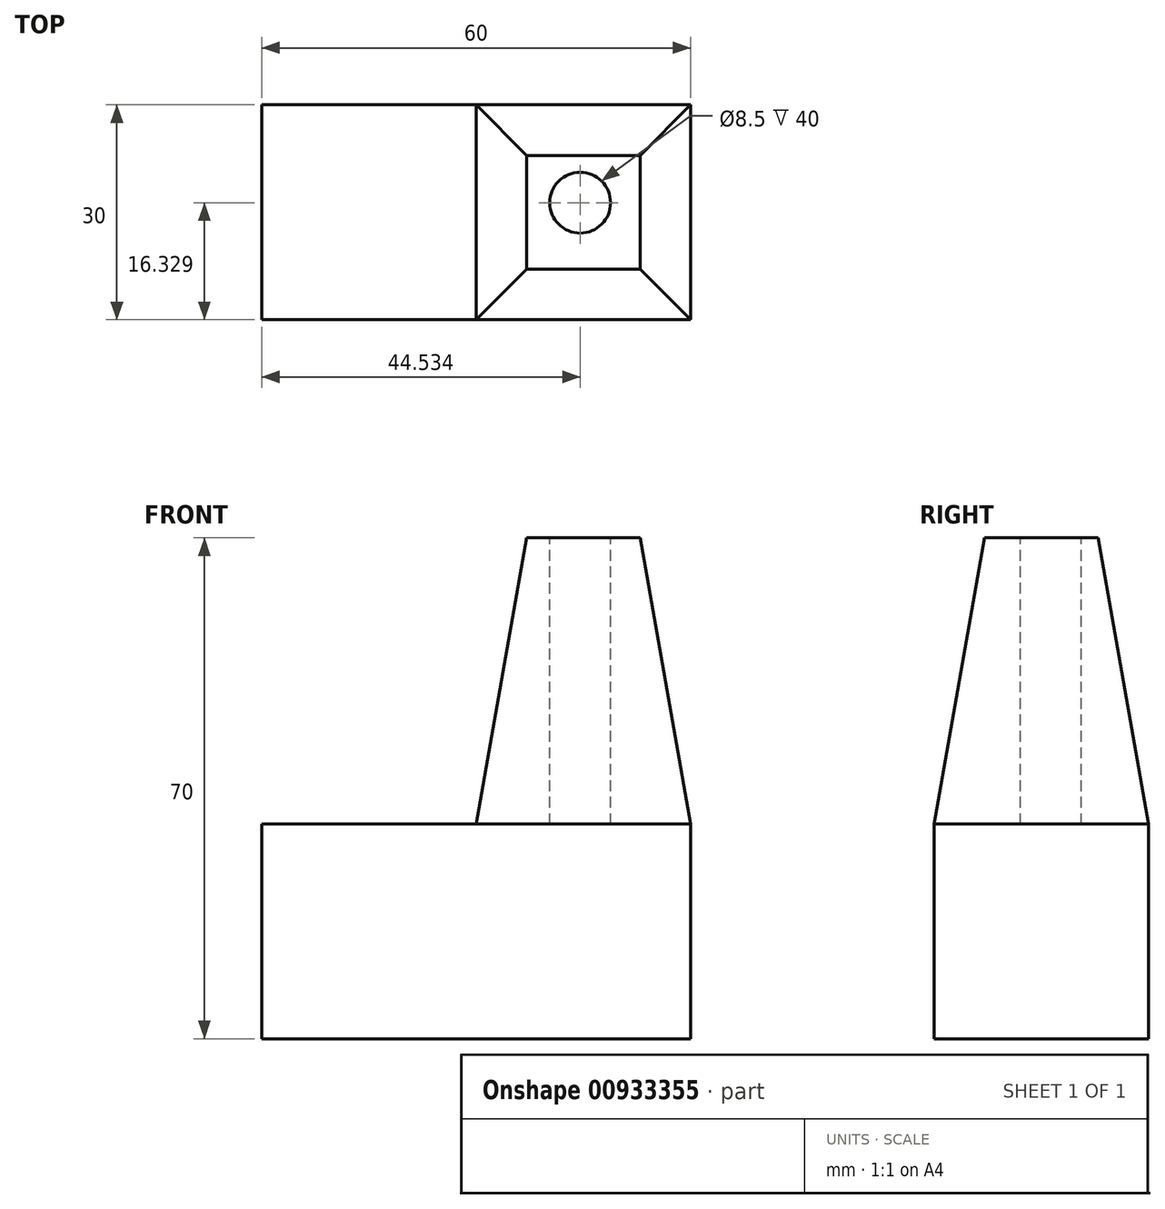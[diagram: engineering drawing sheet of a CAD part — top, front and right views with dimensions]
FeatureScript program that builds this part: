
annotation { "Feature Type Name" : "Feature", "Feature Type Description" : "" }
export const myFeature = defineFeature(function(context is Context, id is Id, definition is map)
    precondition{}
    {
        {
            var Q0;
            Q0=qCreatedBy(makeId("Front.planeOp"),FACE);
            var sketch = newSketch(context, id + "F0", { "sketchPlane" : qUnion([Q0])});
            skLineSegment(sketch, "E0.bottom", {"start": v(30, -15) * mm, "end": v(-30, -15) * mm});
            skLineSegment(sketch, "E0.top", {"start": v(30, 15) * mm, "end": v(-30, 15) * mm});
            skLineSegment(sketch, "E0.left", {"start": v(30, -15) * mm, "end": v(30, 15) * mm});
            skLineSegment(sketch, "E0.right", {"start": v(-30, -15) * mm, "end": v(-30, 15) * mm});
            skPoint(sketch, "E0.middle", {"position": v(0, 0) * mm});
            skSolve(sketch);
        }
        {
            var Q0;
            Q0=makeQuery(id+"F0.imprint","IMPRINT",FACE,{"disambiguationData":[TD([[makeQuery(id+"F0.imprint","IMPRINT",EDGE,{"derivedFrom":sQuery(id+"F0.wireOp",EDGE,"E0.bottom")}),-1.0]])]});
            extrude(context, id + "F1", {"entities" : qUnion([Q0]), "depth" : 30 * mm, "offsetDistance" : 25.4 * mm});
        }
        {
            var Q0;
            Q0=makeQuery(id+"F1.opExtrude","SWEPT_FACE",FACE,{"disambiguationData":[OSD([sQuery(id+"F0.wireOp",EDGE,"E0.top")])]});
            var sketch = newSketch(context, id + "F2", { "sketchPlane" : qUnion([Q0])});
            skLineSegment(sketch, "E1.bottom", {"start": v(30, 0) * mm, "end": v(0, 0) * mm});
            skLineSegment(sketch, "E1.top", {"start": v(30, -30) * mm, "end": v(0, -30) * mm});
            skLineSegment(sketch, "E1.left", {"start": v(30, 0) * mm, "end": v(30, -30) * mm});
            skLineSegment(sketch, "E1.right", {"start": v(0, 0) * mm, "end": v(0, -30) * mm});
            skSolve(sketch);
        }
        {
            var Q0;
            Q0 = qSketchRegion(id + "F2", true);
            extrude(context, id + "F3", {"entities" : qUnion([Q0]), "operationType" : NewBodyOperationType.ADD, "depth" : 40 * mm, "offsetDistance" : 25.4 * mm, "hasDraft" : true, "draftAngle" : 10 * degree, "draftPullDirection" : true});
        }
        {
            var Q0;
            Q0=makeQuery(id+"F3.opExtrude","CAP_FACE",FACE,{"disambiguationData":[OSD([sQuery(id+"F2.wireOp",EDGE,"E1.bottom"),sQuery(id+"F2.wireOp",EDGE,"E1.top"),sQuery(id+"F2.wireOp",EDGE,"E1.left"),sQuery(id+"F2.wireOp",EDGE,"E1.right")])],"isStart":false});
            var sketch = newSketch(context, id + "F4", { "sketchPlane" : qUnion([Q0])});
            skCircle(sketch, "E2", {"center": v(14.53, -13.67) * mm, "radius": 4.25 * mm});
            skSolve(sketch);
        }
        {
            var Q0;
            Q0 = qSketchRegion(id + "F4", true);
            extrude(context, id + "F5", {"entities" : qUnion([Q0]), "operationType" : NewBodyOperationType.REMOVE, "oppositeDirection" : true, "depth" : 40 * mm, "offsetDistance" : 25.4 * mm});
        }
    });
